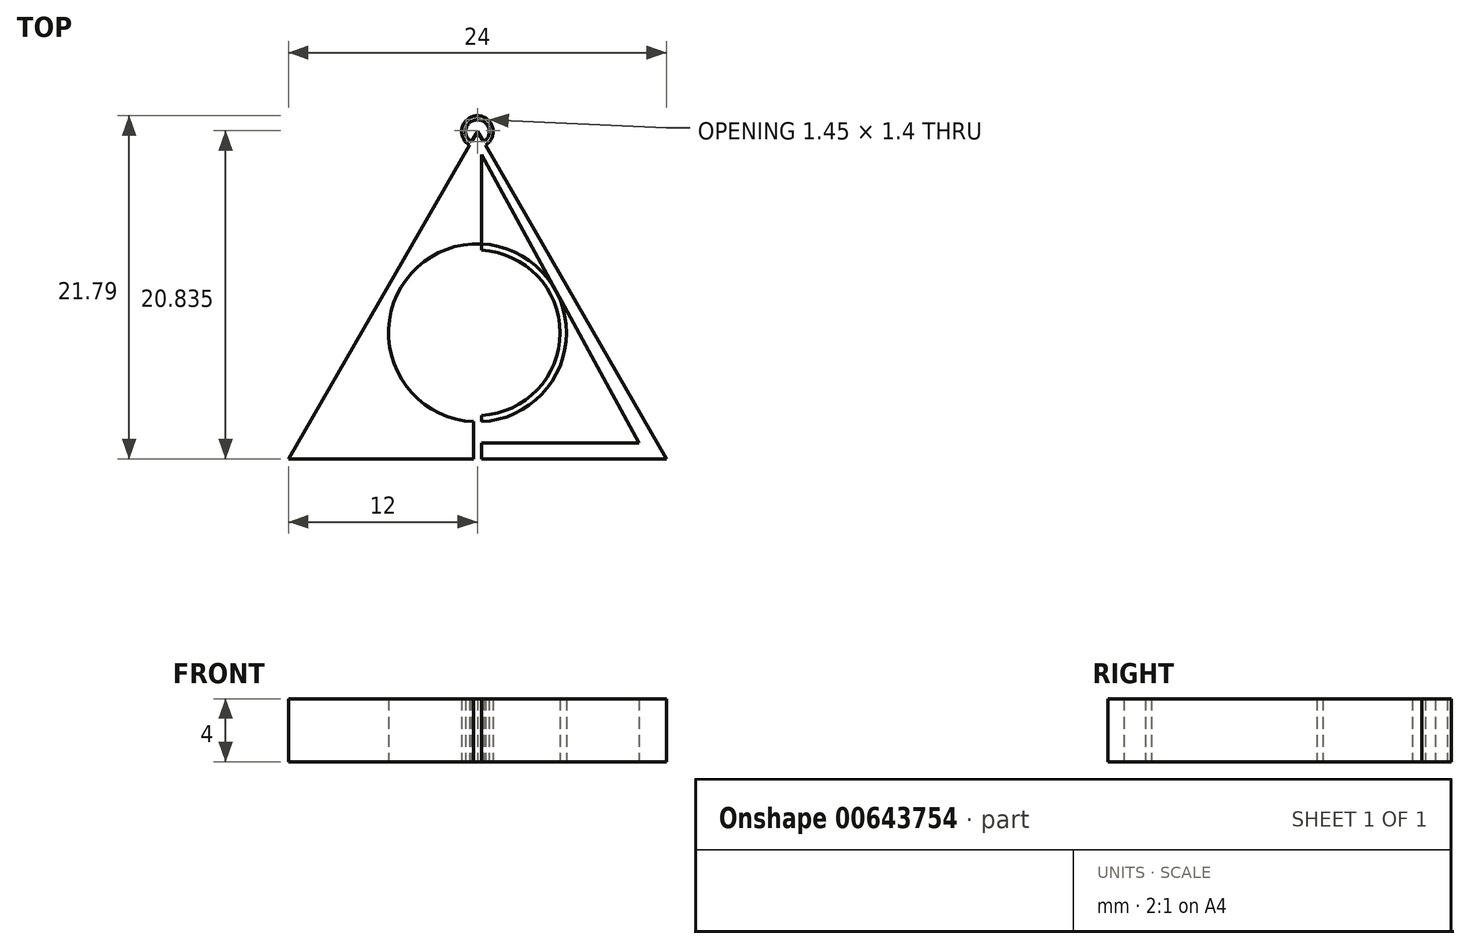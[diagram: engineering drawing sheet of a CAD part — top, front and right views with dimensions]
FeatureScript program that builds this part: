
annotation { "Feature Type Name" : "Feature", "Feature Type Description" : "" }
export const myFeature = defineFeature(function(context is Context, id is Id, definition is map)
    precondition{}
    {
        {
            var Q0;
            Q0=qCreatedBy(makeId("Top.planeOp"),FACE);
            var sketch = newSketch(context, id + "F0", { "sketchPlane" : qUnion([Q0])});
            skLineSegment(sketch, "E0", {"start": v(0, 20.78) * mm, "end": v(-12, 0) * mm});
            skLineSegment(sketch, "E1", {"start": v(-12, 0) * mm, "end": v(12, 0) * mm});
            skLineSegment(sketch, "E2", {"start": v(12, 0) * mm, "end": v(0, 20.78) * mm});
            skPoint(sketch, "E3", {"position": v(0, 19.79) * mm});
            skPoint(sketch, "E4", {"position": v(0, 1) * mm});
            skPoint(sketch, "E5", {"position": v(-10.27, 1) * mm});
            skPoint(sketch, "E6", {"position": v(10.27, 1) * mm});
            skLineSegment(sketch, "E7.bottom", {"start": v(0, 20.78) * mm, "end": v(12, 20.78) * mm});
            skLineSegment(sketch, "E7.top", {"start": v(0, 0) * mm, "end": v(12, 0) * mm});
            skLineSegment(sketch, "E7.left", {"start": v(0, 20.78) * mm, "end": v(0, 0) * mm});
            skLineSegment(sketch, "E7.right", {"start": v(12, 20.78) * mm, "end": v(12, 0) * mm});
            skLineSegment(sketch, "E8.bottom", {"start": v(0, 20.78) * mm, "end": v(-12, 20.78) * mm});
            skLineSegment(sketch, "E8.top", {"start": v(0, 0) * mm, "end": v(-12, 0) * mm});
            skLineSegment(sketch, "E8.right", {"start": v(-12, 20.78) * mm, "end": v(-12, 0) * mm});
            skLineSegment(sketch, "E9", {"start": v(0, 19.79) * mm, "end": v(-10.27, 1) * mm});
            skLineSegment(sketch, "E10", {"start": v(10.27, 1) * mm, "end": v(0, 19.79) * mm});
            skLineSegment(sketch, "E11", {"start": v(-10.27, 1) * mm, "end": v(10.27, 1) * mm});
            skPoint(sketch, "E12", {"position": v(0.25, 19.94) * mm});
            skPoint(sketch, "E13", {"position": v(-0.25, 19.94) * mm});
            skLineSegment(sketch, "E14.bottom", {"start": v(-0.25, 19.94) * mm, "end": v(0.25, 19.94) * mm});
            skLineSegment(sketch, "E14.top", {"start": v(-0.25, 19.94) * mm, "end": v(0.25, 19.94) * mm});
            skLineSegment(sketch, "E14.left", {"start": v(-0.25, 19.94) * mm, "end": v(-0.25, 19.94) * mm});
            skLineSegment(sketch, "E14.right", {"start": v(0.25, 19.94) * mm, "end": v(0.25, 19.94) * mm});
            skLineSegment(sketch, "E15.bottom", {"start": v(0.25, 0) * mm, "end": v(-0.25, 0) * mm});
            skLineSegment(sketch, "E15.top", {"start": v(0.25, 0) * mm, "end": v(-0.25, 0) * mm});
            skLineSegment(sketch, "E15.left", {"start": v(0.25, 0) * mm, "end": v(0.25, 0) * mm});
            skLineSegment(sketch, "E15.right", {"start": v(-0.25, 0) * mm, "end": v(-0.25, 0) * mm});
            skLineSegment(sketch, "E16.top", {"start": v(-0.25, 0) * mm, "end": v(0.25, 0) * mm});
            skLineSegment(sketch, "E16.left", {"start": v(-0.25, 19.94) * mm, "end": v(-0.25, 0) * mm});
            skLineSegment(sketch, "E16.right", {"start": v(0.25, 19.94) * mm, "end": v(0.25, 0) * mm});
            skPoint(sketch, "E17", {"position": v(0, 8) * mm});
            skCircle(sketch, "E18", {"center": v(0, 8) * mm, "radius": 5.65 * mm});
            skCircle(sketch, "E19", {"center": v(0, 8) * mm, "radius": 5.25 * mm});
            skSolve(sketch);
        }
        {
            var Q0;
            {var subQ9=sQuery(id+"F0.wireOp",EDGE,"E0");Q0=makeQuery(id+"F0.imprint","IMPRINT",FACE,{"disambiguationData":[TD([[makeQuery(id+"F0.imprint","IMPRINT",EDGE,{"derivedFrom":subQ9}),1.0]])]});}
            var Q1;
            {var subQ3=sQuery(id+"F0.wireOp",EDGE,"E14.bottom");var subQ5=sQuery(id+"F0.wireOp",EDGE,"E16.left");var subQ6=makeQuery(id+"F0.imprint","INTERSECT",VERTEX,{"derivedFrom":[subQ3,subQ5]});Q1=makeQuery(id+"F0.imprint","IMPRINT",FACE,{"disambiguationData":[TD([[makeQuery(id+"F0.imprint","IMPRINT",EDGE,{"disambiguationData":[TD([[subQ6,-1.0]])],"derivedFrom":subQ3}),-1.0]])]});}
            var Q2;
            {var subQ0=sQuery(id+"F0.wireOp",EDGE,"E9");var subQ5=sQuery(id+"F0.wireOp",EDGE,"E16.left");var subQ6=makeQuery(id+"F0.imprint","INTERSECT",VERTEX,{"derivedFrom":[subQ0,subQ5]});Q2=makeQuery(id+"F0.imprint","IMPRINT",FACE,{"disambiguationData":[TD([[makeQuery(id+"F0.imprint","IMPRINT",EDGE,{"disambiguationData":[TD([[subQ6,-1.0]])],"derivedFrom":subQ5}),1.0]])]});}
            var Q3;
            {var subQ0=sQuery(id+"F0.wireOp",EDGE,"E10");var subQ5=sQuery(id+"F0.wireOp",EDGE,"E16.right");var subQ6=makeQuery(id+"F0.imprint","INTERSECT",VERTEX,{"derivedFrom":[subQ0,subQ5]});Q3=makeQuery(id+"F0.imprint","IMPRINT",FACE,{"disambiguationData":[TD([[makeQuery(id+"F0.imprint","IMPRINT",EDGE,{"disambiguationData":[TD([[subQ6,-1.0]])],"derivedFrom":subQ5}),-1.0]])]});}
            var Q4;
            {var subQ3=sQuery(id+"F0.wireOp",EDGE,"E14.bottom");var subQ5=sQuery(id+"F0.wireOp",EDGE,"E16.right");var subQ7=makeQuery(id+"F0.imprint","INTERSECT",VERTEX,{"derivedFrom":[subQ3,subQ5]});Q4=makeQuery(id+"F0.imprint","IMPRINT",FACE,{"disambiguationData":[TD([[makeQuery(id+"F0.imprint","IMPRINT",EDGE,{"disambiguationData":[TD([[subQ7,1.0]])],"derivedFrom":subQ3}),-1.0]])]});}
            var Q5;
            {var subQ1=sQuery(id+"F0.wireOp",EDGE,"E2");Q5=makeQuery(id+"F0.imprint","IMPRINT",FACE,{"disambiguationData":[TD([[makeQuery(id+"F0.imprint","IMPRINT",EDGE,{"derivedFrom":subQ1}),1.0]])]});}
            var Q6;
            {var subQ0=sQuery(id+"F0.wireOp",EDGE,"E18");var subQ1=sQuery(id+"F0.wireOp",EDGE,"E16.left");var subQ2=makeQuery(id+"F0.imprint","INTERSECT",VERTEX,{"disambiguationData":[OD(0.0)],"derivedFrom":[subQ1,subQ0]});Q6=makeQuery(id+"F0.imprint","IMPRINT",FACE,{"disambiguationData":[TD([[makeQuery(id+"F0.imprint","IMPRINT",EDGE,{"disambiguationData":[TD([[subQ2,-1.0]])],"derivedFrom":subQ1}),-1.0]])]});}
            var Q7;
            {var subQ0=sQuery(id+"F0.wireOp",EDGE,"E19");var subQ1=sQuery(id+"F0.wireOp",EDGE,"E7.left");var subQ2=makeQuery(id+"F0.imprint","INTERSECT",VERTEX,{"disambiguationData":[OD(0.0)],"derivedFrom":[subQ1,subQ0]});Q7=makeQuery(id+"F0.imprint","IMPRINT",FACE,{"disambiguationData":[TD([[makeQuery(id+"F0.imprint","IMPRINT",EDGE,{"disambiguationData":[TD([[subQ2,-1.0]])],"derivedFrom":subQ1}),1.0]])]});}
            var Q8;
            {var subQ0=sQuery(id+"F0.wireOp",EDGE,"E19");var subQ1=sQuery(id+"F0.wireOp",EDGE,"E7.left");var subQ2=makeQuery(id+"F0.imprint","INTERSECT",VERTEX,{"disambiguationData":[OD(0.0)],"derivedFrom":[subQ1,subQ0]});Q8=makeQuery(id+"F0.imprint","IMPRINT",FACE,{"disambiguationData":[TD([[makeQuery(id+"F0.imprint","IMPRINT",EDGE,{"disambiguationData":[TD([[subQ2,-1.0]])],"derivedFrom":subQ1}),-1.0]])]});}
            var Q9;
            {var subQ0=sQuery(id+"F0.wireOp",EDGE,"E18");var subQ1=sQuery(id+"F0.wireOp",EDGE,"E7.left");var subQ2=makeQuery(id+"F0.imprint","INTERSECT",VERTEX,{"disambiguationData":[OD(0.0)],"derivedFrom":[subQ1,subQ0]});Q9=makeQuery(id+"F0.imprint","IMPRINT",FACE,{"disambiguationData":[TD([[makeQuery(id+"F0.imprint","IMPRINT",EDGE,{"disambiguationData":[TD([[subQ2,-1.0]])],"derivedFrom":subQ1}),-1.0]])]});}
            var Q10;
            {var subQ0=sQuery(id+"F0.wireOp",EDGE,"E18");var subQ1=sQuery(id+"F0.wireOp",EDGE,"E7.left");var subQ2=makeQuery(id+"F0.imprint","INTERSECT",VERTEX,{"disambiguationData":[OD(0.0)],"derivedFrom":[subQ1,subQ0]});Q10=makeQuery(id+"F0.imprint","IMPRINT",FACE,{"disambiguationData":[TD([[makeQuery(id+"F0.imprint","IMPRINT",EDGE,{"disambiguationData":[TD([[subQ2,-1.0]])],"derivedFrom":subQ1}),1.0]])]});}
            var Q11;
            {var subQ0=sQuery(id+"F0.wireOp",EDGE,"E18");var subQ1=sQuery(id+"F0.wireOp",EDGE,"E16.right");var subQ2=makeQuery(id+"F0.imprint","INTERSECT",VERTEX,{"disambiguationData":[OD(0.0)],"derivedFrom":[subQ1,subQ0]});Q11=makeQuery(id+"F0.imprint","IMPRINT",FACE,{"disambiguationData":[TD([[makeQuery(id+"F0.imprint","IMPRINT",EDGE,{"disambiguationData":[TD([[subQ2,-1.0]])],"derivedFrom":subQ1}),1.0]])]});}
            var Q12;
            {var subQ0=sQuery(id+"F0.wireOp",EDGE,"E16.top");var subQ1=sQuery(id+"F0.wireOp",EDGE,"E7.left");var subQ2=makeQuery(id+"F0.imprint","INTERSECT",VERTEX,{"derivedFrom":[subQ1,subQ0]});Q12=makeQuery(id+"F0.imprint","IMPRINT",FACE,{"disambiguationData":[TD([[makeQuery(id+"F0.imprint","IMPRINT",EDGE,{"disambiguationData":[TD([[subQ2,1.0]])],"derivedFrom":subQ1}),1.0]])]});}
            var Q13;
            {var subQ0=sQuery(id+"F0.wireOp",EDGE,"E18");var subQ1=sQuery(id+"F0.wireOp",EDGE,"E7.left");var subQ2=makeQuery(id+"F0.imprint","INTERSECT",VERTEX,{"disambiguationData":[OD(1.0)],"derivedFrom":[subQ1,subQ0]});Q13=makeQuery(id+"F0.imprint","IMPRINT",FACE,{"disambiguationData":[TD([[makeQuery(id+"F0.imprint","IMPRINT",EDGE,{"disambiguationData":[TD([[subQ2,-1.0]])],"derivedFrom":subQ1}),-1.0]])]});}
            var Q14;
            {var subQ0=sQuery(id+"F0.wireOp",EDGE,"E18");var subQ1=sQuery(id+"F0.wireOp",EDGE,"E7.left");var subQ2=makeQuery(id+"F0.imprint","INTERSECT",VERTEX,{"disambiguationData":[OD(1.0)],"derivedFrom":[subQ1,subQ0]});Q14=makeQuery(id+"F0.imprint","IMPRINT",FACE,{"disambiguationData":[TD([[makeQuery(id+"F0.imprint","IMPRINT",EDGE,{"disambiguationData":[TD([[subQ2,-1.0]])],"derivedFrom":subQ1}),1.0]])]});}
            var Q15;
            {var subQ0=sQuery(id+"F0.wireOp",EDGE,"E19");var subQ1=sQuery(id+"F0.wireOp",EDGE,"E7.left");var subQ2=makeQuery(id+"F0.imprint","INTERSECT",VERTEX,{"disambiguationData":[OD(1.0)],"derivedFrom":[subQ1,subQ0]});Q15=makeQuery(id+"F0.imprint","IMPRINT",FACE,{"disambiguationData":[TD([[makeQuery(id+"F0.imprint","IMPRINT",EDGE,{"disambiguationData":[TD([[subQ2,-1.0]])],"derivedFrom":subQ1}),-1.0]])]});}
            var Q16;
            {var subQ0=sQuery(id+"F0.wireOp",EDGE,"E19");var subQ1=sQuery(id+"F0.wireOp",EDGE,"E7.left");var subQ2=makeQuery(id+"F0.imprint","INTERSECT",VERTEX,{"disambiguationData":[OD(1.0)],"derivedFrom":[subQ1,subQ0]});Q16=makeQuery(id+"F0.imprint","IMPRINT",FACE,{"disambiguationData":[TD([[makeQuery(id+"F0.imprint","IMPRINT",EDGE,{"disambiguationData":[TD([[subQ2,-1.0]])],"derivedFrom":subQ1}),1.0]])]});}
            var Q17;
            {var subQ0=sQuery(id+"F0.wireOp",EDGE,"E16.top");var subQ1=sQuery(id+"F0.wireOp",EDGE,"E7.left");var subQ2=makeQuery(id+"F0.imprint","INTERSECT",VERTEX,{"derivedFrom":[subQ1,subQ0]});Q17=makeQuery(id+"F0.imprint","IMPRINT",FACE,{"disambiguationData":[TD([[makeQuery(id+"F0.imprint","IMPRINT",EDGE,{"disambiguationData":[TD([[subQ2,1.0]])],"derivedFrom":subQ1}),-1.0]])]});}
            extrude(context, id + "F1", {"entities" : qUnion([Q0, Q1, Q2, Q3, Q4, Q5, Q6, Q7, Q8, Q9, Q10, Q11, Q12, Q13, Q14, Q15, Q16, Q17]), "depth" : 4 * mm, "offsetDistance" : 25 * mm});
        }
        {
            var Q0;
            Q0=qCreatedBy(makeId("Top.planeOp"),FACE);
            var sketch = newSketch(context, id + "F2", { "sketchPlane" : qUnion([Q0])});
            skCircle(sketch, "E20", {"center": v(0, 20.79) * mm, "radius": 1 * mm});
            skCircle(sketch, "E21", {"center": v(0, 20.79) * mm, "radius": 0.75 * mm});
            skSolve(sketch);
        }
        {
            var Q0;
            Q0 = qSketchRegion(id + "F2", true);
            extrude(context, id + "F3", {"entities" : qUnion([Q0]), "operationType" : NewBodyOperationType.ADD, "depth" : 4 * mm, "offsetDistance" : 25 * mm});
        }
    });
